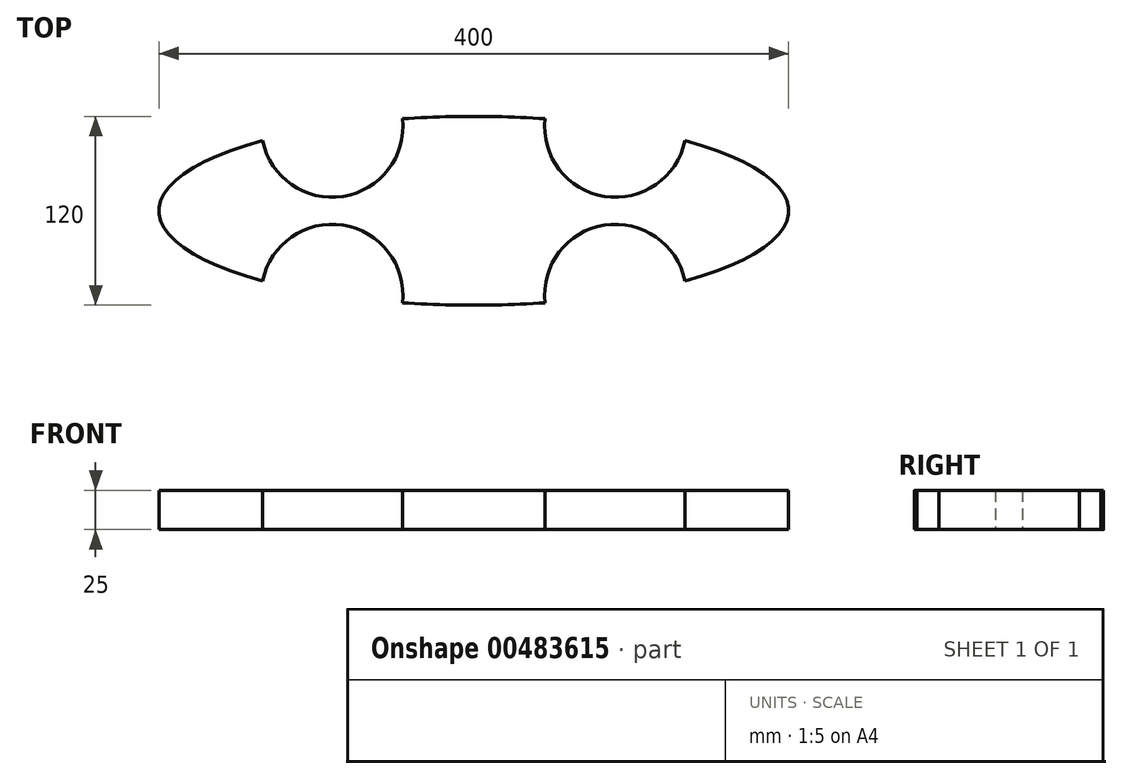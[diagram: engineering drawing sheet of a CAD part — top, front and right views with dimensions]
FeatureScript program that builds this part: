
annotation { "Feature Type Name" : "Feature", "Feature Type Description" : "" }
export const myFeature = defineFeature(function(context is Context, id is Id, definition is map)
    precondition{}
    {
        {
            var Q0;
            Q0=qCreatedBy(makeId("Top.planeOp"),FACE);
            var sketch = newSketch(context, id + "F0", { "sketchPlane" : qUnion([Q0])});
            skLineSegment(sketch, "E0.bottom", {"start": v(200, 100) * mm, "end": v(-200, 100) * mm});
            skLineSegment(sketch, "E0.top", {"start": v(200, -100) * mm, "end": v(-200, -100) * mm});
            skLineSegment(sketch, "E0.left", {"start": v(200, 100) * mm, "end": v(200, -100) * mm});
            skLineSegment(sketch, "E0.right", {"start": v(-200, 100) * mm, "end": v(-200, -100) * mm});
            skPoint(sketch, "E0.middle", {"position": v(0, 0) * mm});
            skLineSegment(sketch, "E1.bottom", {"start": v(200, 60) * mm, "end": v(-200, 60) * mm});
            skLineSegment(sketch, "E1.top", {"start": v(200, -60) * mm, "end": v(-200, -60) * mm});
            skLineSegment(sketch, "E1.left", {"start": v(200, 60) * mm, "end": v(200, -60) * mm});
            skLineSegment(sketch, "E1.right", {"start": v(-200, 60) * mm, "end": v(-200, -60) * mm});
            skPoint(sketch, "E2", {"position": v(200, 0) * mm});
            skPoint(sketch, "E3", {"position": v(0, 60) * mm});
            skEllipse(sketch, "E4", {"center": v(0, 0) * mm, "majorRadius": 200 * mm, "minorRadius": 60 * mm, "majorAxis": v(1, 0)});
            skLineSegment(sketch, "E5.bottom", {"start": v(90, 53.58) * mm, "end": v(-90, 53.58) * mm});
            skLineSegment(sketch, "E5.top", {"start": v(90, -53.58) * mm, "end": v(-90, -53.58) * mm});
            skLineSegment(sketch, "E5.left", {"start": v(90, 53.58) * mm, "end": v(90, -53.58) * mm});
            skLineSegment(sketch, "E5.right", {"start": v(-90, 53.58) * mm, "end": v(-90, -53.58) * mm});
            skCircle(sketch, "E6", {"center": v(-90, 53.58) * mm, "radius": 45 * mm});
            skCircle(sketch, "E7.1.0.0", {"center": v(90, 53.58) * mm, "radius": 45 * mm});
            skLineSegment(sketch, "E7.direction1", {"start": v(-90, 53.58) * mm, "end": v(90, 53.58) * mm, "construction": true});
            skCircle(sketch, "E8.0.1.0", {"center": v(90, -53.58) * mm, "radius": 45 * mm});
            skCircle(sketch, "E8.0.1.1", {"center": v(-90, -53.58) * mm, "radius": 45 * mm});
            skLineSegment(sketch, "E8.direction1", {"start": v(-90, 53.58) * mm, "end": v(-65, 53.58) * mm, "construction": true});
            skLineSegment(sketch, "E8.direction2", {"start": v(-90, 53.58) * mm, "end": v(-90, -53.58) * mm, "construction": true});
            skSolve(sketch);
        }
        {
            var Q0;
            {var subQ5=sQuery(id+"F0.wireOp",EDGE,"E4");var subQ6=makeQuery(id+"F0.imprint","INTERSECT",VERTEX,{"derivedFrom":[sQuery(id+"F0.wireOp",EDGE,"E1.right"),subQ5]});Q0=makeQuery(id+"F0.imprint","IMPRINT",FACE,{"disambiguationData":[TD([[makeQuery(id+"F0.imprint","IMPRINT",EDGE,{"disambiguationData":[TD([[subQ6,1.0]])],"derivedFrom":subQ5}),1.0]])]});}
            var Q1;
            {var subQ5=sQuery(id+"F0.wireOp",EDGE,"E7.1.0.0");var subQ6=sQuery(id+"F0.wireOp",EDGE,"E5.bottom");var subQ7=makeQuery(id+"F0.imprint","INTERSECT",VERTEX,{"derivedFrom":[subQ6,subQ5]});Q1=makeQuery(id+"F0.imprint","IMPRINT",FACE,{"disambiguationData":[TD([[makeQuery(id+"F0.imprint","IMPRINT",EDGE,{"disambiguationData":[TD([[subQ7,-1.0]])],"derivedFrom":subQ6}),1.0]])]});}
            var Q2;
            {var subQ1=sQuery(id+"F0.wireOp",EDGE,"E4");var subQ7=makeQuery(id+"F0.imprint","INTERSECT",VERTEX,{"derivedFrom":[sQuery(id+"F0.wireOp",EDGE,"E1.left"),subQ1]});Q2=makeQuery(id+"F0.imprint","IMPRINT",FACE,{"disambiguationData":[TD([[makeQuery(id+"F0.imprint","IMPRINT",EDGE,{"disambiguationData":[TD([[subQ7,-1.0]])],"derivedFrom":subQ1}),1.0]])]});}
            extrude(context, id + "F1", {"entities" : qUnion([Q0, Q1, Q2]), "depth" : 25 * mm});
        }
    });
